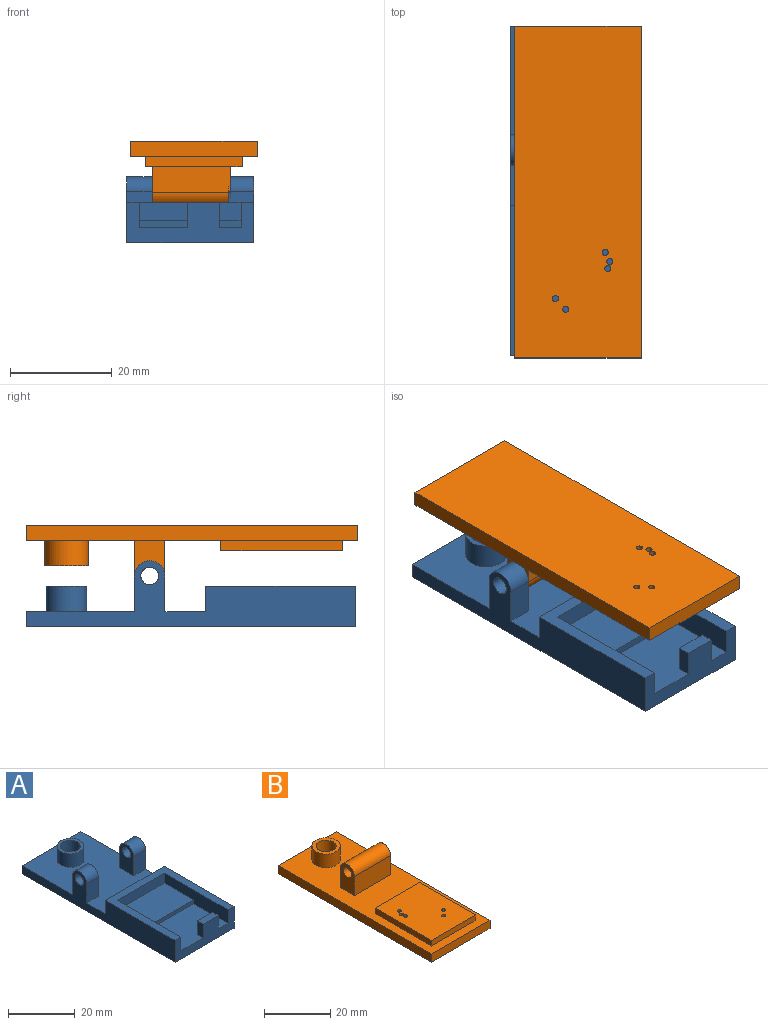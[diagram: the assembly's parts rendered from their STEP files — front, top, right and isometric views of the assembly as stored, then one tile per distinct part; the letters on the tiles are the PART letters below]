
ASSEMBLY  parts=2 mates=1
PART A: 32 faces, bbox 25x64.9x13 mm
  f0: plane 7x5mm, normal (0,1,0), area 35mm2, adj f1,f4,f5,f6
  f1: cylinder r=3mm len=6mm, axis (1,0,0), area 47.1mm2, adj f0,f2,f4,f5
  f2: plane 7x5mm, normal (0,-1,0), area 35mm2, adj f1,f4,f5,f6
  f3: cylinder r=1.75mm len=5mm, axis (1,0,0), area 55mm2, adj f4,f5
  f4: plane 10x6mm, normal (-1,0,0), area 46.5mm2, adj f0,f1,f2,f3,f6
  f5: plane 64.86x13mm, normal (1,0,0), area 388.6mm2, adj f0,f1,f2,f3,f6,f14,f16,f23
  f6: plane 35.36x25mm, normal (0,0,1), area 773.8mm2, adj f0,f2,f4,f5,f16,f17,f18,f20
  f7: plane 27x5mm, normal (1,0,0), area 117.5mm2, adj f9,f10,f14,f24,f29,f30
  f8: plane 27x5mm, normal (-1,0,0), area 117.5mm2, adj f9,f10,f14,f24,f29,f30
  f9: plane 20x3.6mm, normal (0,-1,0), area 72mm2, adj f7,f8,f24,f30
  f10: plane 20x14.5mm, normal (0,0,1), area 274mm2, adj f7,f8,f11,f12,f13,f14,f29
  f11: plane 5x2.5mm, normal (1,0,0), area 12.5mm2, adj f10,f12,f14,f15
  f12: plane 6.4x5mm, normal (0,1,0), area 32mm2, adj f10,f11,f13,f15
  f13: plane 5x2.5mm, normal (-1,0,0), area 12.5mm2, adj f10,f12,f14,f15
  f14: plane 25x8mm, normal (0,-1,0), area 132mm2, adj f5,f7,f8,f10,f11,f13,f15,f17
  f15: plane 6.4x2.5mm, normal (0,0,1), area 16mm2, adj f11,f12,f13,f14
  f16: plane 25x3mm, normal (0,1,0), area 75mm2, adj f5,f6,f17,f31
  f17: plane 64.86x13mm, normal (-1,0,0), area 388.6mm2, adj f6,f14,f16,f18,f19,f20,f21,f23
  f18: plane 7x5mm, normal (0,-1,0), area 35mm2, adj f6,f17,f19,f22
  f19: cylinder r=3mm len=6mm, axis (-1,0,0), area 47.1mm2, adj f17,f18,f20,f22
  f20: plane 7x5mm, normal (0,1,0), area 35mm2, adj f6,f17,f19,f22
  f21: cylinder r=1.75mm len=5mm, axis (-1,0,0), area 55mm2, adj f17,f22
  f22: plane 10x6mm, normal (1,0,0), area 46.5mm2, adj f6,f18,f19,f20,f21
  f23: plane 25x5mm, normal (0,1,0), area 125mm2, adj f5,f6,f17,f24
  f24: plane 29.5x25mm, normal (0,0,1), area 197.5mm2, adj f5,f7,f8,f9,f14,f17,f23
  f25: cylinder r=4mm len=8mm, axis (0,0,-1), area 125.6mm2, adj f6,f27
  f26: cylinder r=3mm len=6mm, axis (0,0,-1), area 94.2mm2, adj f27,f28
  f27: plane 8x8mm, normal (0,0,1), area 21.9mm2, adj f25,f26
  f28: plane 6x6mm, normal (0,0,1), area 28.3mm2, adj f26
  f29: plane 20x1.4mm, normal (0,-1,0), area 28mm2, adj f7,f8,f10,f30
  f30: plane 20x12.5mm, normal (0,0,1), area 250mm2, adj f7,f8,f9,f29
  f31: plane 64.86x25mm, normal (0,0,-1), area 1621.5mm2, adj f5,f14,f16,f17
PART B: 26 faces, bbox 25x65.4x13 mm
  f0: plane 25x3mm, normal (0,-1,0), area 75mm2, adj f1,f7,f9,f10
  f1: plane 65.36x3mm, normal (1,0,0), area 196.1mm2, adj f0,f2,f9,f10
  f2: plane 25x3mm, normal (0,1,0), area 75mm2, adj f1,f7,f9,f10
  f3: cylinder r=0.6mm len=5mm, axis (0,0,1), area 18.8mm2, adj f9,f25
  f4: cylinder r=0.6mm len=5mm, axis (0,0,1), area 18.8mm2, adj f9,f25
  f5: cylinder r=0.6mm len=5mm, axis (0,0,1), area 18.8mm2, adj f9,f25
  f6: cylinder r=0.6mm len=5mm, axis (0,0,1), area 18.8mm2, adj f9,f25
  f7: plane 65.36x3mm, normal (-1,0,0), area 196.1mm2, adj f0,f2,f9,f10
  f8: cylinder r=0.6mm len=5mm, axis (0,0,1), area 18.8mm2, adj f9,f25
  f9: plane 65.36x25mm, normal (0,0,-1), area 1628.3mm2, adj f0,f1,f2,f3,f4,f5,f6,f7
  f10: plane 65.36x25mm, normal (0,0,1), area 1027.7mm2, adj f0,f1,f2,f7,f11,f13,f15,f16
  f11: plane 15.5x7mm, normal (0,-1,0), area 108.5mm2, adj f10,f12,f15,f16
  f12: cylinder r=3mm len=15.5mm, axis (-1,0,0), area 146.1mm2, adj f11,f13,f15,f16
  f13: plane 15.5x7mm, normal (0,1,0), area 108.5mm2, adj f10,f12,f15,f16
  f14: cylinder r=1.75mm len=15.5mm, axis (-1,0,0), area 170.4mm2, adj f15,f16
  f15: plane 10x6mm, normal (1,0,0), area 46.5mm2, adj f10,f11,f12,f13,f14
  f16: plane 10x6mm, normal (-1,0,0), area 46.5mm2, adj f10,f11,f12,f13,f14
  f17: cylinder r=4.27mm len=8.54mm, axis (0,0,-1), area 134.1mm2, adj f10,f19
  f18: plane 6x6mm, normal (0,0,1), area 28.3mm2, adj f20
  f19: plane 8.54x8.54mm, normal (0,0,1), area 28.9mm2, adj f17,f20
  f20: cylinder r=3mm len=6mm, axis (0,0,-1), area 94.2mm2, adj f18,f19
  f21: plane 24x2mm, normal (-1,0,0), area 48mm2, adj f10,f22,f24,f25
  f22: plane 19x2mm, normal (0,-1,0), area 38mm2, adj f10,f21,f23,f25
  f23: plane 24x2mm, normal (1,0,0), area 48mm2, adj f10,f22,f24,f25
  f24: plane 19x2mm, normal (0,1,0), area 38mm2, adj f10,f21,f23,f25
  f25: plane 24x19mm, normal (0,0,1), area 450.3mm2, adj f3,f4,f5,f6,f8,f21,f22,f23
PLACE A t=(-23.29,-62.32,48.81)mm
PLACE B rot(axis=(0,1,0),180deg) t=(-42.09,-62.32,62.81)mm
MATE revolute B.f12 <-> A.f19  axis (-1,0,0) through (-40.79,-24.32,55.81)mm
